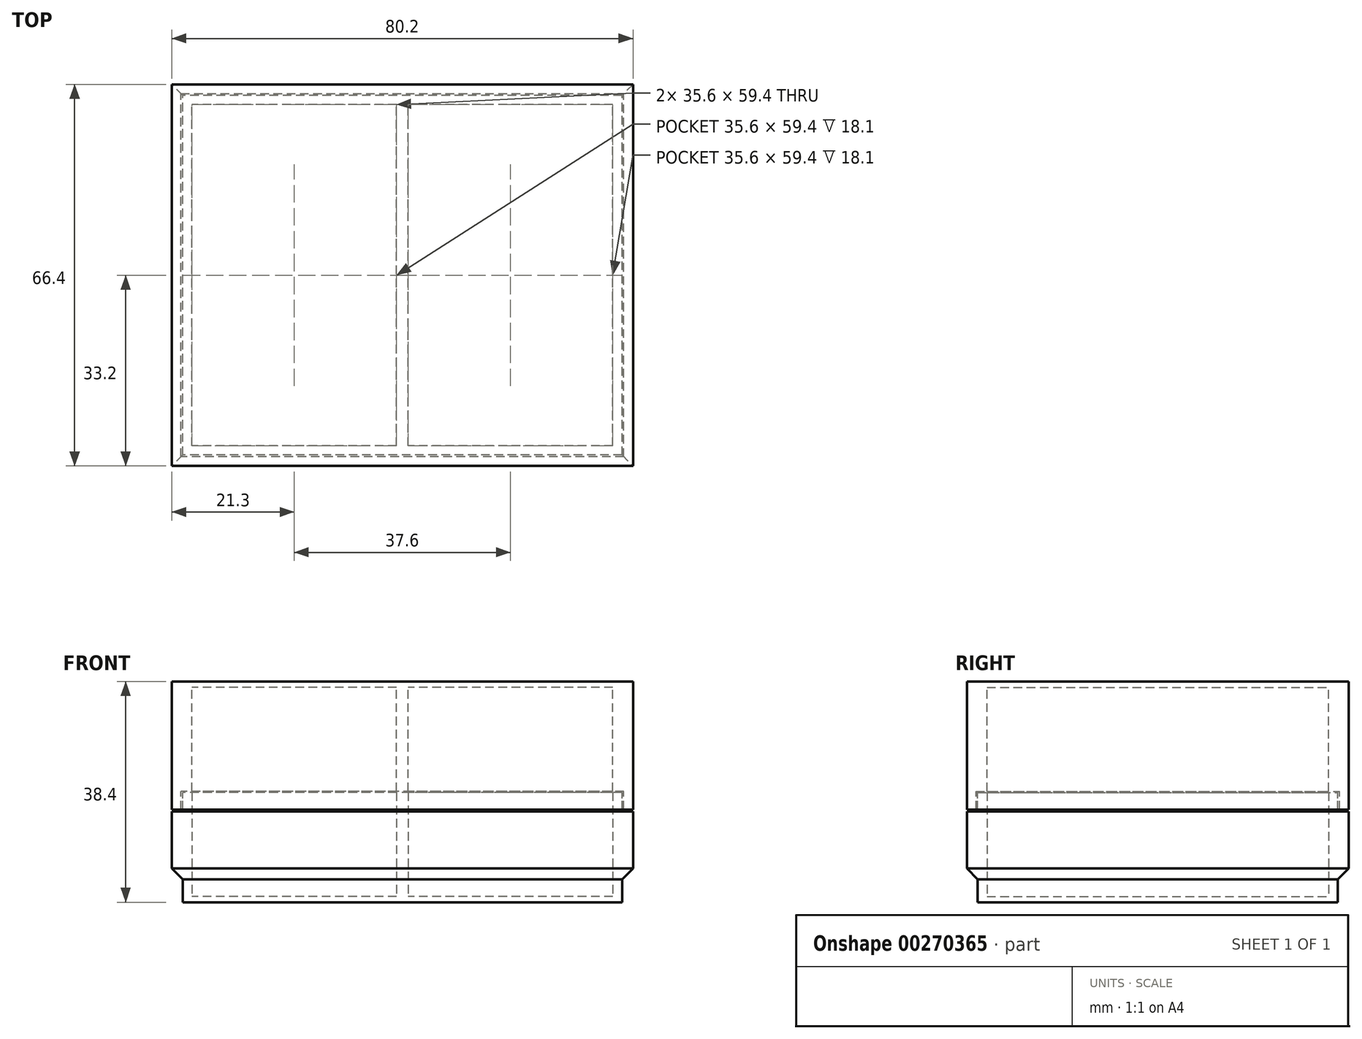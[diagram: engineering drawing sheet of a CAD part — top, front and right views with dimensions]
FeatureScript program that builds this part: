
annotation { "Feature Type Name" : "Feature", "Feature Type Description" : "" }
export const myFeature = defineFeature(function(context is Context, id is Id, definition is map)
    precondition{}
    {
        {
            assignVariable(context, id + "F0", {"name" : "chaff", "anyValue" : .3});
        }
        {
            assignVariable(context, id + "F1", {"name" : "basethick", "anyValue" : 1});
        }
        {
            assignVariable(context, id + "F2", {"name" : "diskdiam", "anyValue" : 35});
        }
        {
            assignVariable(context, id + "F3", {"name" : "lidrimdepth", "anyValue" : 3});
        }
        {
            var Q0;
            Q0=qCreatedBy(makeId("Top.planeOp"),FACE);
            var sketch = newSketch(context, id + "F4", { "sketchPlane" : qUnion([Q0])});
            skLineSegment(sketch, "E0.bottom", {"start": v(40.1, -33.2) * mm, "end": v(-40.1, -33.2) * mm});
            skLineSegment(sketch, "E0.top", {"start": v(40.1, 33.2) * mm, "end": v(-40.1, 33.2) * mm});
            skLineSegment(sketch, "E0.left", {"start": v(40.1, -33.2) * mm, "end": v(40.1, 33.2) * mm});
            skLineSegment(sketch, "E0.right", {"start": v(-40.1, -33.2) * mm, "end": v(-40.1, 33.2) * mm});
            skPoint(sketch, "E0.middle", {"position": v(0, 0) * mm});
            skSolve(sketch);
        }
        {
            var Q0;
            Q0=qSketchRegion(id+"F4",true);
            extrude(context, id + "F5", {"entities" : qUnion([Q0]), "depth" : (getVariable(context, 'basethick')) * mm});
        }
        {
            var Q0;
            Q0=makeQuery(id+"F5.opExtrude","CAP_FACE",FACE,{"disambiguationData":[OSD([sQuery(id+"F4.wireOp",EDGE,"E0.bottom"),sQuery(id+"F4.wireOp",EDGE,"E0.top"),sQuery(id+"F4.wireOp",EDGE,"E0.left"),sQuery(id+"F4.wireOp",EDGE,"E0.right")])],"isStart":false});
            var sketch = newSketch(context, id + "F6", { "sketchPlane" : qUnion([Q0])});
            skLineSegment(sketch, "E1.bottom", {"start": v(36.6, -29.7) * mm, "end": v(-36.6, -29.7) * mm});
            skLineSegment(sketch, "E1.top", {"start": v(36.6, 29.7) * mm, "end": v(-36.6, 29.7) * mm});
            skLineSegment(sketch, "E1.left", {"start": v(36.6, -29.7) * mm, "end": v(36.6, 29.7) * mm});
            skLineSegment(sketch, "E1.right", {"start": v(-36.6, -29.7) * mm, "end": v(-36.6, 29.7) * mm});
            skPoint(sketch, "E1.middle", {"position": v(0, 0) * mm});
            skLineSegment(sketch, "E2", {"start": v(0, 29.7) * mm, "end": v(0, 33.2) * mm, "construction": true});
            skLineSegment(sketch, "E3.0", {"start": v(-40.1, -33.2) * mm, "end": v(-40.1, 33.2) * mm});
            skLineSegment(sketch, "E4.0", {"start": v(40.1, -33.2) * mm, "end": v(-40.1, -33.2) * mm});
            skLineSegment(sketch, "E5.0", {"start": v(40.1, -33.2) * mm, "end": v(40.1, 33.2) * mm});
            skLineSegment(sketch, "E6.0", {"start": v(40.1, 33.2) * mm, "end": v(-40.1, 33.2) * mm});
            skLineSegment(sketch, "E7", {"start": v(-40.1, 0) * mm, "end": v(-36.6, 0) * mm, "construction": true});
            skSolve(sketch);
        }
        {
            var Q0;
            Q0=qSketchRegion(id+"F6",true);
            extrude(context, id + "F7", {"entities" : qUnion([Q0]), "operationType" : NewBodyOperationType.ADD, "depth" : (getVariable(context, 'diskdiam') / 2 + getVariable(context, 'chaff') * 2) * mm});
        }
        {
            var Q0;
            Q0=makeQuery(id+"F7.opExtrude","SWEPT_FACE",FACE,{"disambiguationData":[OSD([sQuery(id+"F6.wireOp",EDGE,"E1.top")])]});
            var sketch = newSketch(context, id + "F8", { "sketchPlane" : qUnion([Q0])});
            skLineSegment(sketch, "E8", {"start": v(-36.6, 19.1) * mm, "end": v(-1, 19.1) * mm, "construction": true});
            skLineSegment(sketch, "E9.bottom", {"start": v(-1, 19.1) * mm, "end": v(1, 19.1) * mm});
            skLineSegment(sketch, "E9.top", {"start": v(-1, 1) * mm, "end": v(1, 1) * mm});
            skLineSegment(sketch, "E9.left", {"start": v(-1, 19.1) * mm, "end": v(-1, 1) * mm});
            skLineSegment(sketch, "E9.right", {"start": v(1, 19.1) * mm, "end": v(1, 1) * mm});
            skLineSegment(sketch, "E10", {"start": v(1, 19.1) * mm, "end": v(36.6, 19.1) * mm, "construction": true});
            skSolve(sketch);
        }
        {
            var Q0;
            Q0=makeQuery(id+"F8.imprint","IMPRINT",FACE,{"disambiguationData":[TD([[makeQuery(id+"F8.imprint","IMPRINT",EDGE,{"derivedFrom":sQuery(id+"F8.wireOp",EDGE,"E9.bottom")}),1.0]])]});
            var Q1;
            Q1=makeQuery(id+"F8.imprint","IMPRINT",FACE,{"disambiguationData":[TD([[makeQuery(id+"F8.imprint","IMPRINT",EDGE,{"derivedFrom":sQuery(id+"F8.wireOp",EDGE,"ARTCU0iS-8ueR-Jnh8-LFhj-PXboDjmYK4JB.bottom")}),1.0]])]});
            var Q2;
            Q2=makeQuery(id+"F8.imprint","IMPRINT",FACE,{"disambiguationData":[TD([[makeQuery(id+"F8.imprint","IMPRINT",EDGE,{"derivedFrom":sQuery(id+"F8.wireOp",EDGE,"1lnmQ6KO-2qVp-VU8h-DFqD-iXou14BrLDrP.bottom")}),1.0]])]});
            var Q3;
            Q3=makeQuery(id+"F7.opExtrude","SWEPT_FACE",FACE,{"disambiguationData":[OSD([sQuery(id+"F6.wireOp",EDGE,"E1.bottom")])]});
            extrude(context, id + "F9", {"entities" : qUnion([Q0, Q1, Q2]), "operationType" : NewBodyOperationType.ADD, "endBound" : BoundingType.UP_TO_SURFACE, "endBoundEntityFace" : qUnion([Q3]), "depth" : 25 * mm});
        }
        {
            var Q0;
            {var subQ0=sQuery(id+"F8.wireOp",EDGE,"b7063ba6-163c-4e90-9692-3a0a1676d49b.0");var subQ1=sQuery(id+"F8.wireOp",EDGE,"5b0bd29a-2a72-4641-92b4-ce3cebaaf724.1.0.1");var subQ2=sQuery(id+"F8.wireOp",EDGE,"5b0bd29a-2a72-4641-92b4-ce3cebaaf724.2.0.1");Q0=makeQuery(id+"F9.boolean.opBoolean","MERGE",FACE,{"derivedFrom":[makeQuery(id+"F7.opExtrude","CAP_FACE",FACE,{"disambiguationData":[OSD([sQuery(id+"F6.wireOp",EDGE,"E1.bottom"),sQuery(id+"F6.wireOp",EDGE,"E1.top"),sQuery(id+"F6.wireOp",EDGE,"E1.left"),sQuery(id+"F6.wireOp",EDGE,"E1.right"),sQuery(id+"F6.wireOp",EDGE,"E3.0"),sQuery(id+"F6.wireOp",EDGE,"E4.0"),sQuery(id+"F6.wireOp",EDGE,"E5.0"),sQuery(id+"F6.wireOp",EDGE,"E6.0")])],"isStart":false}),makeQuery(id+"F9.opExtrude","SWEPT_FACE",FACE,{"disambiguationData":[OSD([subQ0]),TDD([makeQuery(id+"F8.imprint","IMPRINT",EDGE,{"disambiguationData":[TD([[makeQuery(id+"F8.imprint","INTERSECT",VERTEX,{"derivedFrom":[sQuery(id+"F8.wireOp",EDGE,"ed8556cc-012e-414f-a647-4d99696943b9.0"),subQ0]}),-1.0]])],"derivedFrom":subQ0})])]}),makeQuery(id+"F9.opExtrude","SWEPT_FACE",FACE,{"disambiguationData":[OSD([subQ0]),TDD([makeQuery(id+"F8.imprint","IMPRINT",EDGE,{"disambiguationData":[TD([[makeQuery(id+"F8.imprint","INTERSECT",VERTEX,{"disambiguationData":[OD(1.0)],"derivedFrom":[subQ2,subQ0]}),1.0]])],"derivedFrom":subQ0})])]}),makeQuery(id+"F9.opExtrude","SWEPT_FACE",FACE,{"disambiguationData":[OSD([subQ0]),TDD([makeQuery(id+"F8.imprint","IMPRINT",EDGE,{"disambiguationData":[TD([[makeQuery(id+"F8.imprint","INTERSECT",VERTEX,{"disambiguationData":[OD(1.0)],"derivedFrom":[subQ1,subQ0]}),1.0]])],"derivedFrom":subQ0})])]}),makeQuery(id+"F9.opExtrude","SWEPT_FACE",FACE,{"disambiguationData":[OSD([subQ0]),TDD([makeQuery(id+"F8.imprint","IMPRINT",EDGE,{"disambiguationData":[TD([[makeQuery(id+"F8.imprint","INTERSECT",VERTEX,{"derivedFrom":[sQuery(id+"F8.wireOp",EDGE,"CCxmkI6E-hdHg-CZTa-q9Gf-agiM700yoBqG"),subQ0]}),1.0]])],"derivedFrom":subQ0})])]})]});}
            cPlane(context, id + "F10", {"entities" : qUnion([Q0]), "cplaneType" : CPlaneType.OFFSET, "offset" : .1 * mm, "width" : 150 * mm, "height" : 150 * mm});
        }
        {
            var Q0;
            Q0=makeQuery(id+"F5.opExtrude","SWEPT_BODY",BODY,{"disambiguationData":[OSD([sQuery(id+"F4.wireOp",EDGE,"E0.bottom"),sQuery(id+"F4.wireOp",EDGE,"E0.top"),sQuery(id+"F4.wireOp",EDGE,"E0.left"),sQuery(id+"F4.wireOp",EDGE,"E0.right")])]});
            var Q1;
            Q1=qCreatedBy(id+"F10.planeOp",FACE);
            mirror(context, id + "F11", {"entities" : qUnion([Q0]), "mirrorPlane" : qUnion([Q1])});
        }
        {
            var Q0;
            {var subQ0=sQuery(id+"F8.wireOp",EDGE,"b7063ba6-163c-4e90-9692-3a0a1676d49b.0");var subQ1=sQuery(id+"F8.wireOp",EDGE,"5b0bd29a-2a72-4641-92b4-ce3cebaaf724.1.0.1");var subQ2=sQuery(id+"F8.wireOp",EDGE,"5b0bd29a-2a72-4641-92b4-ce3cebaaf724.2.0.1");Q0=makeQuery(id+"F9.boolean.opBoolean","MERGE",FACE,{"derivedFrom":[makeQuery(id+"F7.opExtrude","CAP_FACE",FACE,{"disambiguationData":[OSD([sQuery(id+"F6.wireOp",EDGE,"E1.bottom"),sQuery(id+"F6.wireOp",EDGE,"E1.top"),sQuery(id+"F6.wireOp",EDGE,"E1.left"),sQuery(id+"F6.wireOp",EDGE,"E1.right"),sQuery(id+"F6.wireOp",EDGE,"E3.0"),sQuery(id+"F6.wireOp",EDGE,"E4.0"),sQuery(id+"F6.wireOp",EDGE,"E5.0"),sQuery(id+"F6.wireOp",EDGE,"E6.0")])],"isStart":false}),makeQuery(id+"F9.opExtrude","SWEPT_FACE",FACE,{"disambiguationData":[OSD([subQ0]),TDD([makeQuery(id+"F8.imprint","IMPRINT",EDGE,{"disambiguationData":[TD([[makeQuery(id+"F8.imprint","INTERSECT",VERTEX,{"derivedFrom":[sQuery(id+"F8.wireOp",EDGE,"ed8556cc-012e-414f-a647-4d99696943b9.0"),subQ0]}),-1.0]])],"derivedFrom":subQ0})])]}),makeQuery(id+"F9.opExtrude","SWEPT_FACE",FACE,{"disambiguationData":[OSD([subQ0]),TDD([makeQuery(id+"F8.imprint","IMPRINT",EDGE,{"disambiguationData":[TD([[makeQuery(id+"F8.imprint","INTERSECT",VERTEX,{"disambiguationData":[OD(1.0)],"derivedFrom":[subQ2,subQ0]}),1.0]])],"derivedFrom":subQ0})])]}),makeQuery(id+"F9.opExtrude","SWEPT_FACE",FACE,{"disambiguationData":[OSD([subQ0]),TDD([makeQuery(id+"F8.imprint","IMPRINT",EDGE,{"disambiguationData":[TD([[makeQuery(id+"F8.imprint","INTERSECT",VERTEX,{"disambiguationData":[OD(1.0)],"derivedFrom":[subQ1,subQ0]}),1.0]])],"derivedFrom":subQ0})])]}),makeQuery(id+"F9.opExtrude","SWEPT_FACE",FACE,{"disambiguationData":[OSD([subQ0]),TDD([makeQuery(id+"F8.imprint","IMPRINT",EDGE,{"disambiguationData":[TD([[makeQuery(id+"F8.imprint","INTERSECT",VERTEX,{"derivedFrom":[sQuery(id+"F8.wireOp",EDGE,"CCxmkI6E-hdHg-CZTa-q9Gf-agiM700yoBqG"),subQ0]}),1.0]])],"derivedFrom":subQ0})])]})]});}
            var sketch = newSketch(context, id + "F12", { "sketchPlane" : qUnion([Q0])});
            skLineSegment(sketch, "E11.0", {"start": v(40.1, 33.2) * mm, "end": v(-40.1, 33.2) * mm});
            skLineSegment(sketch, "E12.0", {"start": v(-40.1, -33.2) * mm, "end": v(-40.1, 33.2) * mm});
            skLineSegment(sketch, "E13.0", {"start": v(40.1, -33.2) * mm, "end": v(-40.1, -33.2) * mm});
            skLineSegment(sketch, "E14.0", {"start": v(40.1, -33.2) * mm, "end": v(40.1, 33.2) * mm});
            skLineSegment(sketch, "E15.0", {"start": v(38.2, 31.3) * mm, "end": v(-38.2, 31.3) * mm});
            skLineSegment(sketch, "E15.1", {"start": v(38.2, -31.3) * mm, "end": v(38.2, 31.3) * mm});
            skLineSegment(sketch, "E15.2", {"start": v(38.2, -31.3) * mm, "end": v(-38.2, -31.3) * mm});
            skLineSegment(sketch, "E15.3", {"start": v(-38.2, -31.3) * mm, "end": v(-38.2, 31.3) * mm});
            skSolve(sketch);
        }
        {
            var Q0;
            Q0=makeQuery(id+"F12.imprint","IMPRINT",FACE,{"disambiguationData":[TD([[makeQuery(id+"F12.imprint","IMPRINT",EDGE,{"derivedFrom":sQuery(id+"F12.wireOp",EDGE,"E11.0")}),1.0]])]});
            extrude(context, id + "F13", {"entities" : qUnion([Q0]), "operationType" : NewBodyOperationType.REMOVE, "oppositeDirection" : true, "depth" : (getVariable(context, 'lidrimdepth') + getVariable(context, 'chaff')) * mm});
        }
        {
            var Q0;
            Q0=makeQuery(id+"F5.opExtrude","CAP_FACE",FACE,{"disambiguationData":[OSD([sQuery(id+"F4.wireOp",EDGE,"E0.bottom"),sQuery(id+"F4.wireOp",EDGE,"E0.top"),sQuery(id+"F4.wireOp",EDGE,"E0.left"),sQuery(id+"F4.wireOp",EDGE,"E0.right")])],"isStart":true});
            var sketch = newSketch(context, id + "F14", { "sketchPlane" : qUnion([Q0])});
            skLineSegment(sketch, "E16.0", {"start": v(40.1, 33.2) * mm, "end": v(-40.1, 33.2) * mm});
            skLineSegment(sketch, "E17.0", {"start": v(-40.1, 33.2) * mm, "end": v(-40.1, -33.2) * mm});
            skLineSegment(sketch, "E18.0", {"start": v(40.1, 33.2) * mm, "end": v(40.1, -33.2) * mm});
            skLineSegment(sketch, "E19.0", {"start": v(40.1, -33.2) * mm, "end": v(-40.1, -33.2) * mm});
            skLineSegment(sketch, "E20.0", {"start": v(38.2, 31.3) * mm, "end": v(-38.2, 31.3) * mm});
            skLineSegment(sketch, "E20.1", {"start": v(38.2, 31.3) * mm, "end": v(38.2, -31.3) * mm});
            skLineSegment(sketch, "E20.2", {"start": v(38.2, -31.3) * mm, "end": v(-38.2, -31.3) * mm});
            skLineSegment(sketch, "E20.3", {"start": v(-38.2, 31.3) * mm, "end": v(-38.2, -31.3) * mm});
            skSolve(sketch);
        }
        {
            var Q0;
            Q0=qSketchRegion(id+"F14",true);
            extrude(context, id + "F15", {"entities" : qUnion([Q0]), "operationType" : NewBodyOperationType.REMOVE, "oppositeDirection" : true, "depth" : (getVariable(context, 'lidrimdepth') + 3) * mm});
        }
        {
            var Q0;
            Q0=makeQuery(id+"F15.boolean.opBoolean","COPY",EDGE,{"derivedFrom":makeQuery(id+"F15.opExtrude","CAP_EDGE",EDGE,{"disambiguationData":[OSD([sQuery(id+"F14.wireOp",EDGE,"E20.0")])],"isStart":false})});
            var Q1;
            Q1=makeQuery(id+"F15.boolean.opBoolean","COPY",EDGE,{"derivedFrom":makeQuery(id+"F15.opExtrude","CAP_EDGE",EDGE,{"disambiguationData":[OSD([sQuery(id+"F14.wireOp",EDGE,"E20.3")])],"isStart":false})});
            var Q2;
            Q2=makeQuery(id+"F15.boolean.opBoolean","COPY",EDGE,{"derivedFrom":makeQuery(id+"F15.opExtrude","CAP_EDGE",EDGE,{"disambiguationData":[OSD([sQuery(id+"F14.wireOp",EDGE,"E20.2")])],"isStart":false})});
            var Q3;
            Q3=makeQuery(id+"F15.boolean.opBoolean","COPY",EDGE,{"derivedFrom":makeQuery(id+"F15.opExtrude","CAP_EDGE",EDGE,{"disambiguationData":[OSD([sQuery(id+"F14.wireOp",EDGE,"E20.1")])],"isStart":false})});
            chamfer(context, id + "F16", {"entities" : qUnion([Q0, Q1, Q2, Q3]), "width" : 2 * mm, "tangentPropagation" : true});
        }
        {
            var Q0;
            {var subQ0=sQuery(id+"F8.wireOp",EDGE,"b7063ba6-163c-4e90-9692-3a0a1676d49b.0");var subQ1=sQuery(id+"F8.wireOp",EDGE,"5b0bd29a-2a72-4641-92b4-ce3cebaaf724.1.0.1");var subQ2=sQuery(id+"F8.wireOp",EDGE,"5b0bd29a-2a72-4641-92b4-ce3cebaaf724.2.0.1");Q0=makeQuery(id+"F11.opPattern","COPY",FACE,{"derivedFrom":makeQuery(id+"F9.boolean.opBoolean","MERGE",FACE,{"derivedFrom":[makeQuery(id+"F7.opExtrude","CAP_FACE",FACE,{"disambiguationData":[OSD([sQuery(id+"F6.wireOp",EDGE,"E1.bottom"),sQuery(id+"F6.wireOp",EDGE,"E1.top"),sQuery(id+"F6.wireOp",EDGE,"E1.left"),sQuery(id+"F6.wireOp",EDGE,"E1.right"),sQuery(id+"F6.wireOp",EDGE,"E3.0"),sQuery(id+"F6.wireOp",EDGE,"E4.0"),sQuery(id+"F6.wireOp",EDGE,"E5.0"),sQuery(id+"F6.wireOp",EDGE,"E6.0")])],"isStart":false}),makeQuery(id+"F9.opExtrude","SWEPT_FACE",FACE,{"disambiguationData":[OSD([subQ0]),TDD([makeQuery(id+"F8.imprint","IMPRINT",EDGE,{"disambiguationData":[TD([[makeQuery(id+"F8.imprint","INTERSECT",VERTEX,{"derivedFrom":[sQuery(id+"F8.wireOp",EDGE,"ed8556cc-012e-414f-a647-4d99696943b9.0"),subQ0]}),-1.0]])],"derivedFrom":subQ0})])]}),makeQuery(id+"F9.opExtrude","SWEPT_FACE",FACE,{"disambiguationData":[OSD([subQ0]),TDD([makeQuery(id+"F8.imprint","IMPRINT",EDGE,{"disambiguationData":[TD([[makeQuery(id+"F8.imprint","INTERSECT",VERTEX,{"disambiguationData":[OD(1.0)],"derivedFrom":[subQ2,subQ0]}),1.0]])],"derivedFrom":subQ0})])]}),makeQuery(id+"F9.opExtrude","SWEPT_FACE",FACE,{"disambiguationData":[OSD([subQ0]),TDD([makeQuery(id+"F8.imprint","IMPRINT",EDGE,{"disambiguationData":[TD([[makeQuery(id+"F8.imprint","INTERSECT",VERTEX,{"disambiguationData":[OD(1.0)],"derivedFrom":[subQ1,subQ0]}),1.0]])],"derivedFrom":subQ0})])]}),makeQuery(id+"F9.opExtrude","SWEPT_FACE",FACE,{"disambiguationData":[OSD([subQ0]),TDD([makeQuery(id+"F8.imprint","IMPRINT",EDGE,{"disambiguationData":[TD([[makeQuery(id+"F8.imprint","INTERSECT",VERTEX,{"derivedFrom":[sQuery(id+"F8.wireOp",EDGE,"CCxmkI6E-hdHg-CZTa-q9Gf-agiM700yoBqG"),subQ0]}),1.0]])],"derivedFrom":subQ0})])]})]}),"instanceName":"1"});}
            var sketch = newSketch(context, id + "F17", { "sketchPlane" : qUnion([Q0])});
            skPoint(sketch, "E21.0", {"position": v(-36.6, 29.7) * mm});
            skPoint(sketch, "E22.0", {"position": v(36.6, -29.7) * mm});
            skPoint(sketch, "E23.0", {"position": v(-36.6, -29.7) * mm});
            skLineSegment(sketch, "E24", {"start": v(36.6, 29.7) * mm, "end": v(-36.6, 29.7) * mm, "construction": true});
            skLineSegment(sketch, "E25", {"start": v(-36.6, -29.7) * mm, "end": v(36.6, -29.7) * mm, "construction": true});
            skLineSegment(sketch, "E26", {"start": v(36.6, 29.7) * mm, "end": v(36.6, -29.7) * mm, "construction": true});
            skLineSegment(sketch, "E27", {"start": v(-36.6, 29.7) * mm, "end": v(-36.6, -29.7) * mm, "construction": true});
            skLineSegment(sketch, "E28.0", {"start": v(38.5, 31.6) * mm, "end": v(-38.5, 31.6) * mm});
            skLineSegment(sketch, "E28.1", {"start": v(38.5, 31.6) * mm, "end": v(38.5, -31.6) * mm});
            skLineSegment(sketch, "E28.2", {"start": v(-38.5, -31.6) * mm, "end": v(38.5, -31.6) * mm});
            skLineSegment(sketch, "E28.3", {"start": v(-38.5, 31.6) * mm, "end": v(-38.5, -31.6) * mm});
            skLineSegment(sketch, "E29.0", {"start": v(40.1, 33.2) * mm, "end": v(-40.1, 33.2) * mm});
            skLineSegment(sketch, "E30.0", {"start": v(40.1, 33.2) * mm, "end": v(40.1, -33.2) * mm});
            skLineSegment(sketch, "E31.0", {"start": v(40.1, -33.2) * mm, "end": v(-40.1, -33.2) * mm});
            skLineSegment(sketch, "E32.0", {"start": v(-40.1, 33.2) * mm, "end": v(-40.1, -33.2) * mm});
            skPoint(sketch, "E33", {"position": v(36.6, 29.7) * mm});
            skSolve(sketch);
        }
        {
            var Q0;
            Q0=qSketchRegion(id+"F17",true);
            extrude(context, id + "F18", {"entities" : qUnion([Q0]), "operationType" : NewBodyOperationType.ADD, "depth" : 3.2 * mm});
        }
    });
